# Revit family: BOS-LineaCompact-lSidW-STW_Familie
name_source: partatom
category: Türen
revit_build: Autodesk Revit 2017 (Build: 20160225_1515(x64)
units: mm (PartAtom-declared; Revit-internal decimal feet)

## family parameters
Basisbauteil = Wand
Beim Laden mit Abzugskörper schneiden = Nein
Gemeinsam genutzt = Nein
Immer vertikal = Ja
Raumberechnungspunkt = Ja

## types (4) — shared parameters
BE max. = 100 mm  [stored 0.328084 ft]
Bauelement = BOS Stahlzarge
Beplankungsabstand = 7 mm  [stored 0.0229659 ft]
Beplankungsstärke hinten = 25 mm  [stored 0.082021 ft]
Beplankungsstärke vorne = 25 mm  [stored 0.082021 ft]
Beschreibung = Schiebetürzarge für in der Wand laufende Schiebetüren (LineaCompact) für Ständerwerk
Funktion = Innen
Glastürblattstärke = 8 mm  [stored 0.0262467 ft]
Hersteller = BOS GmbH Best Of Steel, Lütkenfelde 4, D-48282 Emsdetten
Holztürblattstärke = 40 mm  [stored 0.131234 ft]
Info-Texte sichtbar = Ja
Information in English = Nein
LDB max. = 1186 mm  [stored 3.89108 ft]
LDB min. = 561 mm
LDH effektiv max. = 2433 mm  [stored 7.98228 ft]
LDH effektiv min. = 1985 mm  [stored 6.51247 ft]
Laufkastenbreite = 54 mm  [stored 0.177165 ft]
MW max. = 175 mm  [stored 0.574147 ft]
MW min. = 125 mm  [stored 0.410105 ft]
Material = grundiert, feuerverzinktes Feinblech nach DIN EN 10143
Material - Bürstendichtung = <Nach Kategorie>
Material - Führungszapfen = <Nach Kategorie>
Material - Laufschiene = <Nach Kategorie>
Material - Türgriff = <Nach Kategorie>
Material - Zarge = <Nach Kategorie>
Profilblechstärke = 2 mm  [stored 0.00656168 ft]
Putzwinkel max. = 28 mm  [stored 0.0918635 ft]
Putzwinkel min. = 10 mm  [stored 0.0328084 ft]
Spiegel hinten max. = 80 mm  [stored 0.262467 ft]
Spiegel hinten min. = 30 mm  [stored 0.0984252 ft]
Spiegel vorne max. = 80 mm  [stored 0.262467 ft]
Spiegel vorne min. = 30 mm  [stored 0.0984252 ft]
Technische Infos rund um die Stahlzarge = www.BestOfSteel.de/tools-downloads/technische-infos-rund-um-die-stahlzarge/
Türblatteinstand hinten = 36 mm  [stored 0.11811 ft]
Türblatteinstand vorne = 13 mm
URL = www.BestOfSteel.de/stahlzargen/zargen-fuer-schiebetueren/lineacompact/lineacompact/
Zargenblechstärke = 1.5 mm  [stored 0.00492126 ft]
zero-valued in all types: Breite, Dicke, Rohbaubreite, Rohbauhöhe

## per-type parameters (varying)
| type | ALU 100 BOS | ALU 80 BOS | Bürstendichtung | Glastürblatt | Holztürblatt | Material - Türblatt | lSidW mit ALU 100 BOS Glas | lSidW mit ALU 100 BOS Holz | lSidW mit ALU 80 BOS Glas | lSidW mit ALU 80 BOS Holz |
| lSidW mit ALU 80 BOS Holz | Nein | Ja | Nein | Nein | Ja | <Nach Kategorie> | Nein | Nein | Nein | Ja |
| lSidW mit ALU 100 BOS Holz | Ja | Nein | Nein | Nein | Ja | <Nach Kategorie> | Nein | Ja | Nein | Nein |
| lSidW mit ALU 100 BOS Glas | Ja | Nein | Ja | Ja | Nein | Glas | Ja | Nein | Nein | Nein |
| lSidW mit ALU 80 BOS Glas | Nein | Ja | Ja | Ja | Nein | Glas | Nein | Nein | Ja | Nein |

note: column(s) folded — value = type name in every type: Modell

note: [stored X ft] marks values corroborated as IEEE doubles in the binary element streams (Revit-internal decimal feet)
